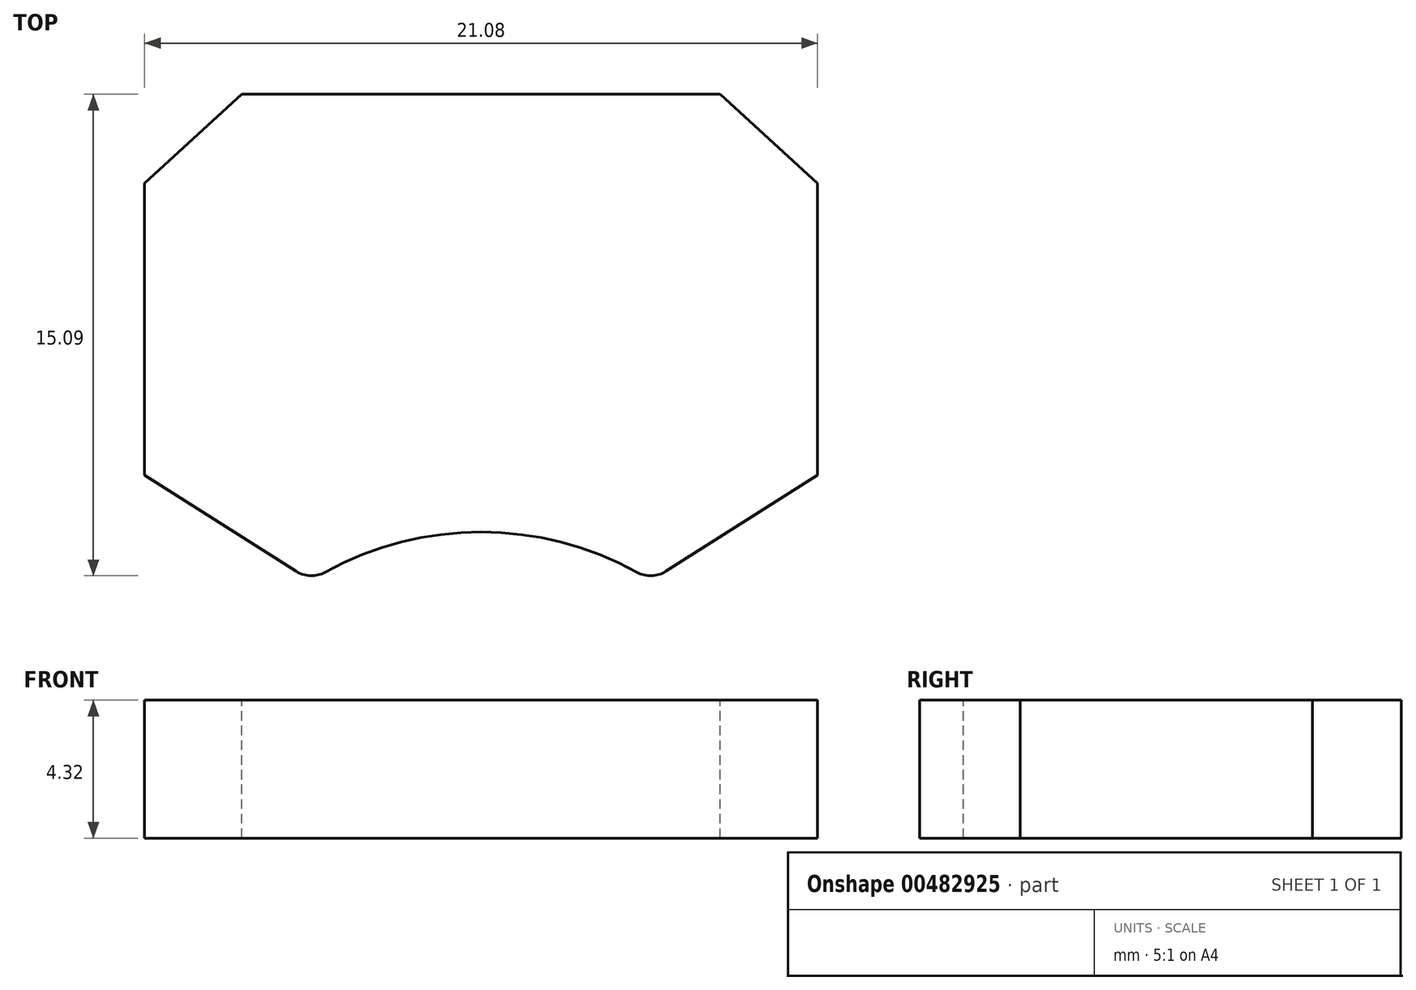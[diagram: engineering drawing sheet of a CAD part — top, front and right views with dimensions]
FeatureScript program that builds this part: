
annotation { "Feature Type Name" : "Feature", "Feature Type Description" : "" }
export const myFeature = defineFeature(function(context is Context, id is Id, definition is map)
    precondition{}
    {
        {
            var Q0;
            Q0=qCreatedBy(makeId("Top.planeOp"),FACE);
            var sketch = newSketch(context, id + "F0", { "sketchPlane" : qUnion([Q0])});
            skLineSegment(sketch, "E0.bottom", {"start": v(7.49, 7.62) * mm, "end": v(0, 7.62) * mm});
            skLineSegment(sketch, "E0.left", {"start": v(10.54, 4.83) * mm, "end": v(10.54, -4.32) * mm});
            skPoint(sketch, "E0.middle", {"position": v(0, 0) * mm});
            skLineSegment(sketch, "E1", {"start": v(10.54, 4.83) * mm, "end": v(7.49, 7.62) * mm});
            skLineSegment(sketch, "E2", {"start": v(0, 7.62) * mm, "end": v(0, -7.62) * mm, "construction": true});
            skLineSegment(sketch, "E3", {"start": v(0, -6.1) * mm, "end": v(7.73, -6.1) * mm, "construction": true});
            skArc(sketch, "E4", {"start": v(4.89, -7.36) * mm, "mid": v(2.52, -6.42) * mm, "end": v(0, -6.1) * mm});
            skLineSegment(sketch, "E5", {"start": v(5.8, -7.33) * mm, "end": v(10.54, -4.32) * mm});
            skPoint(sketch, "E6.visualSharp", {"position": v(5.33, -7.62) * mm});
            skArc(sketch, "E6.filletArc", {"start": v(4.89, -7.36) * mm, "mid": v(5.34, -7.47) * mm, "end": v(5.8, -7.33) * mm});
            skLineSegment(sketch, "E7.MirrorCS", {"start": v(-7.49, 7.62) * mm, "end": v(0, 7.62) * mm});
            skLineSegment(sketch, "E8.MirrorCS", {"start": v(-10.54, 4.83) * mm, "end": v(-7.49, 7.62) * mm});
            skLineSegment(sketch, "E9.MirrorCS", {"start": v(-10.54, 4.83) * mm, "end": v(-10.54, -4.32) * mm});
            skLineSegment(sketch, "E10.MirrorCS", {"start": v(-5.8, -7.33) * mm, "end": v(-10.54, -4.32) * mm});
            skArc(sketch, "E11.MirrorCS", {"start": v(-4.89, -7.36) * mm, "mid": v(-2.52, -6.42) * mm, "end": v(0, -6.1) * mm});
            skArc(sketch, "E12.MirrorCS", {"start": v(-4.89, -7.36) * mm, "mid": v(-5.34, -7.47) * mm, "end": v(-5.8, -7.33) * mm});
            skSolve(sketch);
        }
        {
            var Q0;
            Q0 = qSketchRegion(id + "F0", true);
            extrude(context, id + "F1", {"entities" : qUnion([Q0]), "oppositeDirection" : true, "depth" : 4.32 * mm});
        }
    });
